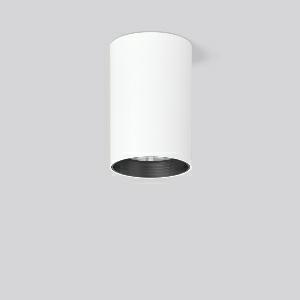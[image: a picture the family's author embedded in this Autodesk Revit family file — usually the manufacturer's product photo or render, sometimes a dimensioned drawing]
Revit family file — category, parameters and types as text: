
# Revit family: heledon_maxi_a_931236_002_76_026d
name_source: partatom
category: Lighting Fixtures
units: mm (PartAtom-declared; Revit-internal decimal feet)

## family parameters
Cut with Voids When Loaded = No
Host = Face
Light Source = No
Part Type = Normal
Room Calculation Point = No
Round Connector Dimension = Use Diameter
Shared = No

## types (1)
- HELEDON maxi A (1 x LED Modul 932 fresh meat, 1800 lm, 3200)
    Apparent Load = 33 VA
    Approval mark = CE
    CIE Flux Codes = 96 99 100 100 100
    Color Rendering = 90
    Color Temperature = 3200
    Default Elevation = 1800 mm  [stored 5.90551 ft]
    Description = Series: HELEDON maxi
Cylindrical surface-mounted downlight. Housing: die-cast aluminium, powder-coated. Internal ceiling frame polycarbonate with bayonet mounting. Black plastic ring and recessed LED to prevent glare from the side. Optical assembly with lens made of plastic (polycarbonate) for the best homogeneous light distribution - can be changed without tools. Special LED for illumination of meat included. Suitable for Ceiling mounting. Easy installation with a separate ceiling frame with bayonet mounting and plug connection. Driver integrated. Connected via plug-in connector. High quality converter without flickering and stroboscopic effect. The following accessories can be mounted without use of tools: interchangeable lenses, decorative glasses, honeycomb louvre, clear and frosted diffusers, white interchangeable plastic ring. 
Colour: traffic white, matt (RAL 9016)
Diameter: 123 mm
Height: 183 mm
Lamp: LED
Socket: without socket
Colour temperature: fresh meat
System power: 33 W
Rated luminous flux: 1800 lm
Luminous efficiency: 55 lm/W
Control gear: Converter, dimmable, DALI
Protection class: I
Type of protection: IP 20
    Height = 183 mm
    Lamp = 1 x LED Modul 932 fresh meat
    Lamp Light Flux = 1800 lm
    Lamp count = 1
    Length = 123 mm
    Lifetime = 50000 h
    Luminous efficacy = 55 lm/W
    Manufacturer = RZB
    ModVariant = No
    Model = 931236.002.76
    Mounting Place = Ceiling
    Mounting Type = Surface mounted
    Number of Poles = 1
    OnlyDefault = Yes
    Power Factor = 1
    Product Name = HELEDON maxi A
    Product group = Surface mounted downlights
    ProductGroupID = 302
    Protection Class = Protection class I
    Protection Degree = IP 20
    RLX_Detail_Level = 1
    RLX_Emergency_Light_Flux = 0 lm
    RLX_Emergency_Type = 0
    RLX_Emergency_Type_DB = No
    RlxData = <blob elided: 97585 chars, md5=dc16d039>
    Socket = socket
    Standby Power = 0 W
    System Light Flux = 1800 lm
    System Power = 33 W
    Type Comments = Product without accessories
    Type Image = 931193.002.jpg
    URL = http://relux.com
    VarID = ---
    Voltage = 230 V
    Voltage Range = 220-240 V
    Weight = 0.00 kg
    Width = 0 mm  [stored 0 ft]

note: [stored X ft] marks values corroborated as IEEE doubles in the binary element streams (Revit-internal decimal feet)

## geometry (parser evidence)
native form markers: Blend x4, Sweep x12
no freeform markers — native parametric forms only
